# Revit family: IS_iLifeS_T4734_BIM_GB
name_source: partatom
category: Plumbing Fixtures
units: mm (PartAtom-declared; Revit-internal decimal feet)

## family parameters
Always vertical = No
Cut with Voids When Loaded = No
OmniClass Number = 23.45.05.21.11.11
OmniClass Title = Water Operated Water Closets
Part Type = Normal
Room Calculation Point = No
Round Connector Dimension = Use Diameter
Shared = No
Work Plane-Based = No

## types (1)
- T473401 - i.life S,WC Cistern, 6/ 3 L - White
    Accessories = https://www.idealstandard.co.uk
    AreaUnits = millimetres
    AssetType = Fixed
    BIMObjectName = IS_IdealStandard_WC cisterns_i.lifeS_T4734
    BIMobject category = Toilet Cisterns
    BIMobject category code = toilet-cisterns
    BIMobject main category = Sanitary
    BIMobject main category code = sanitary
    BarCode = 8014140491422
    Brand = Ideal Standard
    Brand url = http://www.idealstandard.co.uk
    Category = Sanitary
    CisternCapacity = 0.00 m³
    Color = White
    ConnectionType = Plumbing
    Cost = 0 $
    CurrencyUnit = £
    CurrentRevision = 1
    Date of publishing = 27/05/2022
    Description = Ideal Standard, i.life S, cistern, bottom inlet, trim mounted, pre-adjusted, 6/3 l,for compact bowl cc &btw i.life S and cc btw I.life A, white, in carton box, EU pallet
    DurationUnit = Years
    Edition number = 1
    ElementType = Fixed
    ExpectedLife = 99
    Features = Ideal Standard, i.life S, cistern, bottom inlet, trim mounted, pre-adjusted, 6/3 l,for compact bowl cc &btw i.life S and cc btw I.life A, white, in carton box, EU pallet
    Finish = White
    FlushRate = 0.00 m³
    GTIN code = https://8014140491422
    Help = https://www.idealstandard.co.uk
    IFC Classification = Sanitary Terminal
    IfcExportAs = IfcSanitaryTerminalType
    IfcExportType = TOILETPAN
    Installation instructions = https://www.idealstandard.co.uk
    InstallationInstructions = https://www.idealstandard.co.uk
    IsAutomaticFlush = No
    LinearUnits = Millimetres
    MainColor = White
    MaintenanceInformation = https://www.idealstandard.co.uk
    Manufacturer = Ideal Standard
    Manufacturer name = Ideal Standard
    ManufacturerURL = https://www.idealstandard.co.uk
    Material = Vitrous China
    Material main = Vitrous China
    Model = T473401
    ModelNumber = T473401
    ModelReference = i.life S,WC Cistern, 6/ 3 L
    NBS Reference Code = 45-35-70/383
    NBS Reference Description = WC cisterns
    Name = WC cisterns_i.lifeS_T4734_IdealStandard
    NettWeight = 14.5
    NominalDepth = 148 mm
    NominalHeight = 398 mm
    NominalLength = 148 mm
    NominalWidth = 364 mm
    OmniClass Code = 23-31 19 00
    OmniClass Description = Toilets
    PredefinedType = Sanitary
    Product Guid = b2645e6d-7e29-43ea-a460-8506094dde35
    Product SKU = T4734
    Product certification = https://www.idealstandard.co.uk
    Product data url = https://bimobject.com
    Product family = I.life S
    Product group = Sanitry: Cisterns
    Product name = i.life S,WC Cistern, 6/ 3 L
    Product url = https://www.idealstandard.co.uk
    ProductInformation = https://www.idealstandard.co.uk
    QR code = http://bimobject.com
    ReplacementCost = 0
    Shape = Sculpture
    Size = 364 x 148 x 398 mm
    Space = Internal
    SpareParts = https://www.idealstandard.co.uk
    Technical description = https://www.idealstandard.co.uk
    UNSPSC Code = 301815
    URL = https://www.idealstandard.co.uk
    Uniclass 2015 Code = Pr_40_20_93_89
    Uniclass 2015 Name = WC cisterns
    Uniclass2015Code = Pr_40_20_93_89
    Uniclass2015Title = WC cisterns
    Uniclass2015Version = v.25
    Version = 1
    VolumeUnits = Litres
    WRASURL = https://www.wrasapprovals.co.uk
    WarrantyDescription = manufacturer warranty
    WarrantyDurationUnit = years
    Youtube clip = https://www.youtube.com

## geometry (parser evidence)
native form markers: Sweep x1
no freeform markers — native parametric forms only
